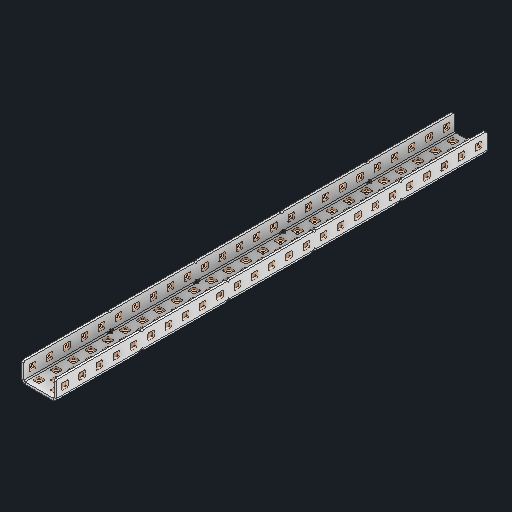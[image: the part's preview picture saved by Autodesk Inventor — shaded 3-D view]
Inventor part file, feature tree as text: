
AUTODESK INVENTOR PART (.ipt)
format: ipt  version: 2024 (Build 280153000, 153)  size: 1,556,480 bytes
history: native  units: in
note: dims shown in document units (in); Inventor stores cm internally (conversion verified against a paired STEP export)
features: other x132, extrude x123, sheet_metal_op x11, pattern_linear x2, mirror x1, chamfer x1, sketch x1
ambient origin geometry x8: Origin, YZ Plane, XZ Plane, XY Plane, X Axis, Y Axis, Z Axis, Center Point
bodies: Solid1 (feature_tree), Body (feature_tree)
feature tree (271):
  sheet_metal_op  "Flanges"
  other  "Flange Pattern Plane"
  other  "Flange Pattern Sketch"
  sheet_metal_op  "Flange Pattern"
  sheet_metal_op  "Body Pattern"
  pattern_linear  "Center Pattern"  Spacing1=12.5in  [1 undecoded]
  other  "Arc Length"
  mirror  "Notch Mirror"
  pattern_linear  "Notch Pattern"  Spacing1=0.0625in  [1 undecoded]
  chamfer  "End Chamfer"
  extrude  "Half Cut"  Depth=0.0625in
  other  "Plate1"
  sketch  "Sketch2"  dims[d0=1.0in d1=12.5in d2=0.0625in d3=0.0625in d4=0.0312in d5=0.125in d6=0.0625in d7=0.5in d8=90.0deg d9=0.0312in d10=0.25in d11=0.0625in d12=0.0625in d16=0.182in d17=0.02in d18=0.0625in d19=0.0in d20=0.25in d21=0.25in d38=9.8425in d40=0.5in d41=0.7874in d43=1.0in d46=0.172in d47=1.0in d48=0.0in d49=0.182in d50=0.02in d51=0.25in d52=0.25in d53=0.0625in d54=0.0in d55=0.172in d56=1.0in d57=0.0in d58=0.25in d60=9.8425in d62=0.5in d63=0.7874in d65=0.5in d85=0.1473in d86=0.1782in d88=0.04in d89=0.0625in d90=0.0in d91=0.04in d92=0.0491in d95=2.5in d96=0.04in d97=0.25in d98=45.0deg d99=0.25in d100=0.5in d101=0.0in d102=2.497in d106=0.182in d107=0.02in d108=0.5in d109=0.5in d110=0.0625in d111=0.0in d112=0.172in d113=0.5in d114=0.0in d117=0.5in d118=0.5in d119=0.5in]
  other  "Plate2"
  sheet_metal_op  "Bend1"
  sheet_metal_op  "Corner1"
  other  "Srf1"
  other  "Srf2"
  other  "Srf91"
  sheet_metal_op  "Body Pattern Sketch"
  other  "Srf92"
  other  "Srf786"
  other  "Srf823"
  other  "Srf824"
  other  "Srf825"
  other  "Srf826"
  other  "Srf827"
  other  "Srf828"
  other  "Srf829"
  other  "Srf856"
  other  "Srf857"
  other  "Srf858"
  other  "Srf859"
  other  "Srf860"
  other  "Srf861"
  other  "Srf862"
  other  "Srf889"
  other  "Srf890"
  other  "Srf891"
  other  "Srf892"
  other  "Srf893"
  other  "Srf894"
  other  "Srf895"
  other  "Srf896"
  other  "Srf922"
  other  "Srf923"
  other  "Srf924"
  other  "Srf925"
  other  "Srf926"
  other  "Srf959"
  other  "Srf960"
  other  "Srf961"
  other  "Srf962"
  other  "Srf963"
  other  "Srf996"
  other  "Srf997"
  other  "Srf998"
  other  "Srf999"
  other  "Srf1000"
  other  "Srf1143"
  other  "Srf1144"
  other  "Srf1145"
  other  "Srf1146"
  other  "Srf1147"
  other  "Srf1148"
  other  "Srf1149"
  other  "Srf1150"
  other  "Srf1151"
  other  "Srf1152"
  other  "Srf1153"
  other  "Srf1154"
  other  "Srf1155"
  other  "Srf1156"
  other  "Srf1157"
  other  "Srf1158"
  other  "Srf1159"
  other  "Srf1160"
  other  "Srf1161"
  other  "Srf1162"
  other  "Srf1163"
  other  "Srf1164"
  other  "Srf1165"
  other  "Srf1166"
  other  "Srf1167"
  other  "Srf1168"
  other  "Srf1169"
  other  "Srf1170"
  other  "Srf1171"
  other  "Srf1172"
  other  "Srf1173"
  other  "Srf1174"
  other  "Srf1175"
  other  "Srf1176"
  other  "Srf1177"
  other  "Srf1178"
  other  "Srf1199"
  other  "Srf1200"
  other  "Srf1201"
  other  "Srf1202"
  other  "Srf1203"
  other  "Srf1204"
  other  "Srf1205"
  other  "Srf1206"
  other  "Srf1207"
  other  "Srf1208"
  other  "Srf1209"
  other  "Srf1210"
  other  "Srf1211"
  other  "Srf1212"
  other  "Srf1213"
  other  "Srf1214"
  other  "Srf1215"
  other  "Srf1216"
  other  "Srf1217"
  other  "Srf1218"
  other  "Srf1219"
  other  "Srf1220"
  other  "Srf1221"
  other  "Srf1222"
  other  "Srf1223"
  other  "Srf1224"
  other  "Srf1225"
  other  "Srf1226"
  other  "Srf1227"
  other  "Srf1228"
  other  "Srf1229"
  other  "Srf1230"
  other  "Srf1231"
  other  "Srf1232"
  other  "Srf1233"
  other  "Srf1234"
  other  "Srf1255"
  other  "Srf1256"
  other  "Srf1257"
  other  "Srf1258"
  other  "Srf1259"
  other  "Srf1260"
  other  "Srf1261"
  other  "Srf1262"
  other  "Srf1263"
  other  "Srf1264"
  other  "Srf1265"
  sheet_metal_op  "Flange Stamp"
  sheet_metal_op  "Flange Circle"
  sheet_metal_op  "Body Stamp"
  sheet_metal_op  "Body Circle"
  other  "Center Stamp"
  other  "Center Circle"
  sheet_metal_op  "Notch"
  extrude  "ExtrusionSrf2"  Depth=0.0312in
  extrude  "ExtrusionSrf92"  Depth=0.5in
  extrude  "ExtrusionSrf823"  Depth=0.0625in
  extrude  "ExtrusionSrf824"  Depth=0.5in TaperAngle=90.0deg
  extrude  "ExtrusionSrf825"  Depth=0.5in
  extrude  "ExtrusionSrf826"  Depth=0.0625in
  extrude  "ExtrusionSrf827"  Depth=0.0625in
  extrude  "ExtrusionSrf828"  Depth=0.5in
  extrude  "ExtrusionSrf829"  Depth=0.02in
  extrude  "ExtrusionSrf856"  Depth=0.0625in
  extrude  "ExtrusionSrf857"  TaperAngle=0.0deg  [1 undecoded]
  extrude  "ExtrusionSrf858"  Depth=0.5in
  extrude  "ExtrusionSrf859"  Depth=0.5in
  extrude  "ExtrusionSrf860"  Depth=0.5in
  extrude  "ExtrusionSrf861"  Depth=0.5in
  extrude  "ExtrusionSrf862"  Depth=1.0in TaperAngle=0.0deg
  extrude  "ExtrusionSrf889"  Depth=0.5in
  extrude  "ExtrusionSrf890"  Depth=0.02in
  extrude  "ExtrusionSrf891"  Depth=0.5in
  extrude  "ExtrusionSrf892"  Depth=0.5in
  extrude  "ExtrusionSrf893"  Depth=0.0625in
  extrude  "ExtrusionSrf894"  TaperAngle=0.0deg  [1 undecoded]
  extrude  "ExtrusionSrf895"  Depth=0.5in
  extrude  "ExtrusionSrf896"  Depth=1.0in TaperAngle=0.0deg
  extrude  "ExtrusionSrf922"  Depth=0.5in
  extrude  "ExtrusionSrf923"  Depth=0.5in
  extrude  "ExtrusionSrf924"  Depth=0.5in
  extrude  "ExtrusionSrf925"  Depth=0.5in
  extrude  "ExtrusionSrf926"  Depth=0.5in
  extrude  "ExtrusionSrf959"  Depth=0.5in
  extrude  "ExtrusionSrf960"  Depth=0.0625in
  extrude  "ExtrusionSrf961"  TaperAngle=0.0deg  [1 undecoded]
  extrude  "ExtrusionSrf962"  Depth=0.5in
  extrude  "ExtrusionSrf963"  Depth=0.5in
  extrude  "ExtrusionSrf996"  Depth=2.5in
  extrude  "ExtrusionSrf997"  Depth=0.5in TaperAngle=45.0deg
  extrude  "ExtrusionSrf998"  Depth=0.5in
  extrude  "ExtrusionSrf999"  Depth=0.5in TaperAngle=0.0deg
  extrude  "ExtrusionSrf1000"  Depth=0.5in
  extrude  "ExtrusionSrf1143"  Depth=0.5in
  extrude  "ExtrusionSrf1144"  Depth=0.02in
  extrude  "ExtrusionSrf1145"  Depth=0.5in
  extrude  "ExtrusionSrf1146"  Depth=0.5in
  extrude  "ExtrusionSrf1147"  Depth=0.0625in
  extrude  "ExtrusionSrf1148"  TaperAngle=0.0deg  [1 undecoded]
  extrude  "ExtrusionSrf1149"  Depth=0.5in
  extrude  "ExtrusionSrf1150"  Depth=0.5in TaperAngle=0.0deg
  extrude  "ExtrusionSrf1151"  Depth=0.5in
  extrude  "ExtrusionSrf1152"  Depth=0.5in
  extrude  "ExtrusionSrf1153"  Depth=0.5in
  extrude  "ExtrusionSrf1154"  [1 undecoded]
  extrude  "ExtrusionSrf1155"  [1 undecoded]
  extrude  "ExtrusionSrf1156"  [1 undecoded]
  extrude  "ExtrusionSrf1157"  [1 undecoded]
  extrude  "ExtrusionSrf1158"  [1 undecoded]
  extrude  "ExtrusionSrf1159"  [1 undecoded]
  extrude  "ExtrusionSrf1160"  [1 undecoded]
  extrude  "ExtrusionSrf1161"  [1 undecoded]
  extrude  "ExtrusionSrf1162"  [1 undecoded]
  extrude  "ExtrusionSrf1163"  [1 undecoded]
  extrude  "ExtrusionSrf1164"  [1 undecoded]
  extrude  "ExtrusionSrf1165"  [1 undecoded]
  extrude  "ExtrusionSrf1166"  [1 undecoded]
  extrude  "ExtrusionSrf1167"  [1 undecoded]
  extrude  "ExtrusionSrf1168"  [1 undecoded]
  extrude  "ExtrusionSrf1169"  [1 undecoded]
  extrude  "ExtrusionSrf1170"  [1 undecoded]
  extrude  "ExtrusionSrf1171"  [1 undecoded]
  extrude  "ExtrusionSrf1172"  [1 undecoded]
  extrude  "ExtrusionSrf1173"  [1 undecoded]
  extrude  "ExtrusionSrf1174"  [1 undecoded]
  extrude  "ExtrusionSrf1175"  [1 undecoded]
  extrude  "ExtrusionSrf1176"  [1 undecoded]
  extrude  "ExtrusionSrf1177"  [1 undecoded]
  extrude  "ExtrusionSrf1178"  [1 undecoded]
  extrude  "ExtrusionSrf1199"  [1 undecoded]
  extrude  "ExtrusionSrf1200"  [1 undecoded]
  extrude  "ExtrusionSrf1201"  [1 undecoded]
  extrude  "ExtrusionSrf1202"  [1 undecoded]
  extrude  "ExtrusionSrf1203"  [1 undecoded]
  extrude  "ExtrusionSrf1204"  [1 undecoded]
  extrude  "ExtrusionSrf1205"  [1 undecoded]
  extrude  "ExtrusionSrf1206"  [1 undecoded]
  extrude  "ExtrusionSrf1207"  [1 undecoded]
  extrude  "ExtrusionSrf1208"  [1 undecoded]
  extrude  "ExtrusionSrf1209"  [1 undecoded]
  extrude  "ExtrusionSrf1210"  [1 undecoded]
  extrude  "ExtrusionSrf1211"  [1 undecoded]
  extrude  "ExtrusionSrf1212"  [1 undecoded]
  extrude  "ExtrusionSrf1213"  [1 undecoded]
  extrude  "ExtrusionSrf1214"  [1 undecoded]
  extrude  "ExtrusionSrf1215"  [1 undecoded]
  extrude  "ExtrusionSrf1216"  [1 undecoded]
  extrude  "ExtrusionSrf1217"  [1 undecoded]
  extrude  "ExtrusionSrf1218"  [1 undecoded]
  extrude  "ExtrusionSrf1219"  [1 undecoded]
  extrude  "ExtrusionSrf1220"  [1 undecoded]
  extrude  "ExtrusionSrf1221"  [1 undecoded]
  extrude  "ExtrusionSrf1222"  [1 undecoded]
  extrude  "ExtrusionSrf1223"  [1 undecoded]
  extrude  "ExtrusionSrf1224"  [1 undecoded]
  extrude  "ExtrusionSrf1225"  [1 undecoded]
  extrude  "ExtrusionSrf1226"  [1 undecoded]
  extrude  "ExtrusionSrf1227"  [1 undecoded]
  extrude  "ExtrusionSrf1228"  [1 undecoded]
  extrude  "ExtrusionSrf1229"  [1 undecoded]
  extrude  "ExtrusionSrf1230"  [1 undecoded]
  extrude  "ExtrusionSrf1231"  [1 undecoded]
  extrude  "ExtrusionSrf1232"  [1 undecoded]
  extrude  "ExtrusionSrf1233"  [1 undecoded]
  extrude  "ExtrusionSrf1234"  [1 undecoded]
  extrude  "ExtrusionSrf1255"  [1 undecoded]
  extrude  "ExtrusionSrf1256"  [1 undecoded]
  extrude  "ExtrusionSrf1257"  [1 undecoded]
  extrude  "ExtrusionSrf1258"  [1 undecoded]
  extrude  "ExtrusionSrf1259"  [1 undecoded]
  extrude  "ExtrusionSrf1260"  [1 undecoded]
  extrude  "ExtrusionSrf1261"  [1 undecoded]
  extrude  "ExtrusionSrf1262"  [1 undecoded]
  extrude  "ExtrusionSrf1263"  [1 undecoded]
  extrude  "ExtrusionSrf1264"  [1 undecoded]
  extrude  "ExtrusionSrf1265"  [1 undecoded]
note: 78 required parameter values undecoded (feature->parameter linkage not recoverable at this tier; creation-order binding heuristic only, values carry confidence <= 0.55)
